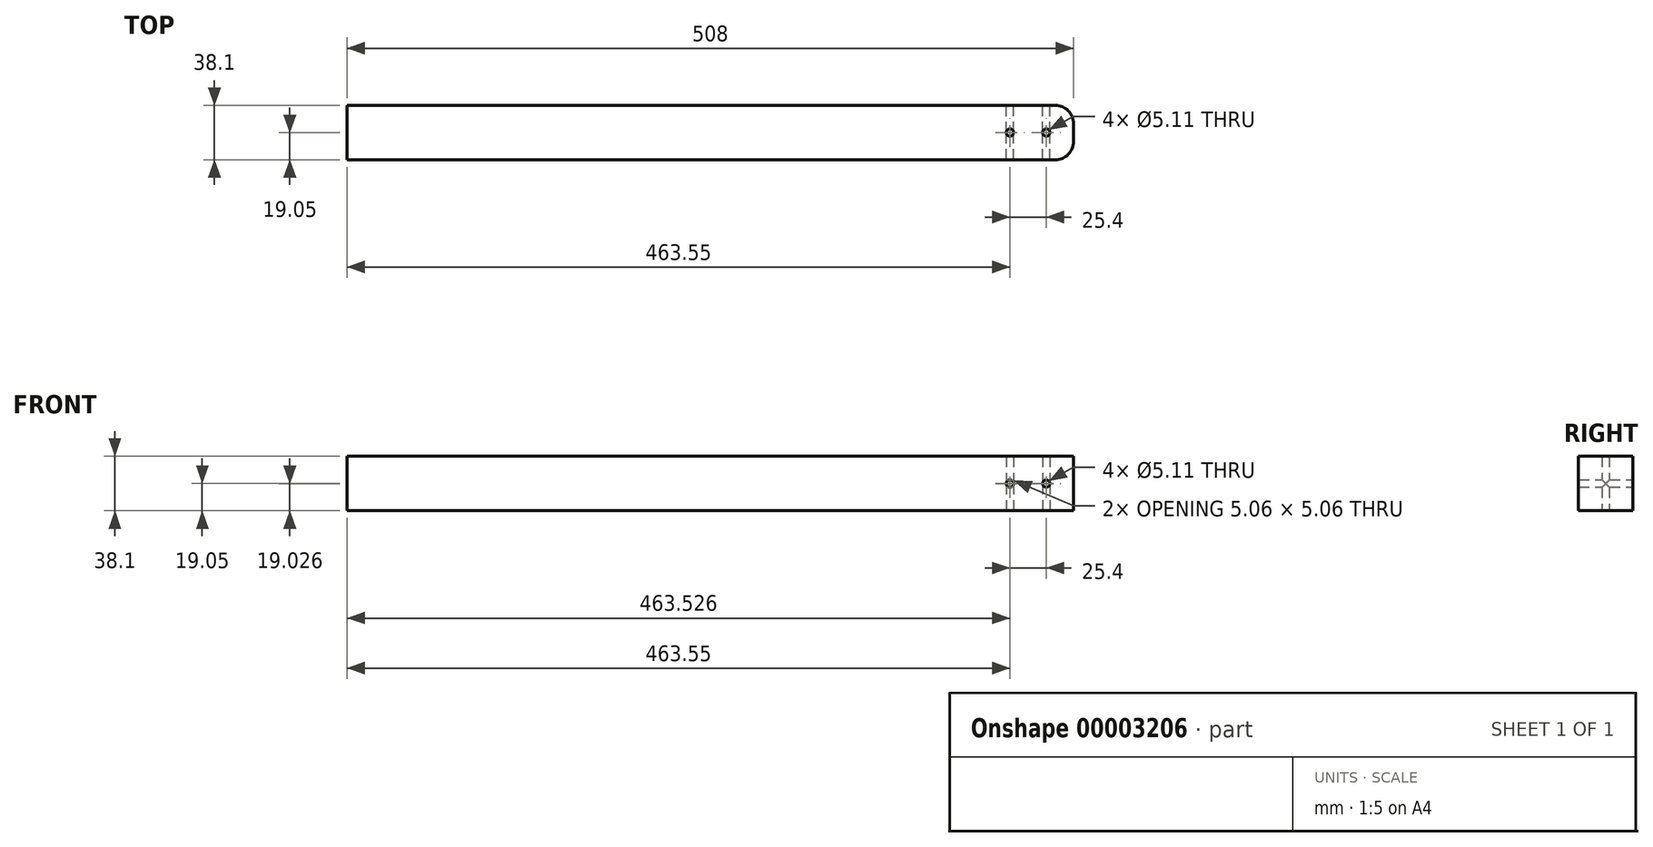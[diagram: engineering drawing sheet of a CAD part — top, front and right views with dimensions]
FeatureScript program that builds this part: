
annotation { "Feature Type Name" : "Feature", "Feature Type Description" : "" }
export const myFeature = defineFeature(function(context is Context, id is Id, definition is map)
    precondition{}
    {
        {
            var Q0;
            Q0=qCreatedBy(makeId("Front.planeOp"),FACE);
            var sketch = newSketch(context, id + "F0", { "sketchPlane" : qUnion([Q0])});
            skLineSegment(sketch, "E0", {"start": v(0, 0) * mm, "end": v(0, -38.1) * mm});
            skLineSegment(sketch, "E1", {"start": v(0, -38.1) * mm, "end": v(508, -38.1) * mm});
            skLineSegment(sketch, "E2", {"start": v(508, -38.1) * mm, "end": v(508, 0) * mm});
            skLineSegment(sketch, "E3", {"start": v(508, 0) * mm, "end": v(0, 0) * mm});
            skLineSegment(sketch, "E4", {"start": v(508, -19.05) * mm, "end": v(320.2, -19.05) * mm, "construction": true});
            skLineSegment(sketch, "E5", {"start": v(488.95, 0) * mm, "end": v(488.95, -38.1) * mm, "construction": true});
            skLineSegment(sketch, "E6", {"start": v(463.55, 0) * mm, "end": v(463.55, -38.1) * mm, "construction": true});
            skCircle(sketch, "E7", {"center": v(463.55, -19.05) * mm, "radius": 2.55 * mm});
            skCircle(sketch, "E8", {"center": v(488.95, -19.05) * mm, "radius": 2.55 * mm});
            skSolve(sketch);
        }
        {
            var Q0;
            Q0=makeQuery(id+"F0.imprint","IMPRINT",FACE,{"disambiguationData":[TD([[makeQuery(id+"F0.imprint","IMPRINT",EDGE,{"derivedFrom":sQuery(id+"F0.wireOp",EDGE,"E0")}),1.0]])]});
            extrude(context, id + "F1", {"entities" : qUnion([Q0]), "endBound" : BoundingType.SYMMETRIC, "depth" : 38.1 * mm});
        }
        {
            var Q0;
            Q0=makeQuery(id+"F1.opExtrude","SWEPT_FACE",FACE,{"disambiguationData":[OSD([sQuery(id+"F0.wireOp",EDGE,"E1")])]});
            var sketch = newSketch(context, id + "F2", { "sketchPlane" : qUnion([Q0])});
            skLineSegment(sketch, "E9", {"start": v(508, 0) * mm, "end": v(309.48, 0) * mm, "construction": true});
            skLineSegment(sketch, "E10", {"start": v(488.95, 19.05) * mm, "end": v(488.95, -19.05) * mm, "construction": true});
            skLineSegment(sketch, "E11", {"start": v(463.55, 19.05) * mm, "end": v(463.55, -19.05) * mm, "construction": true});
            skCircle(sketch, "E12", {"center": v(463.55, 0) * mm, "radius": 2.55 * mm});
            skCircle(sketch, "E13", {"center": v(488.95, 0) * mm, "radius": 2.55 * mm});
            skSolve(sketch);
        }
        {
            var Q0;
            Q0=makeQuery(id+"F2.imprint","IMPRINT",FACE,{"disambiguationData":[TD([[makeQuery(id+"F2.imprint","IMPRINT",EDGE,{"derivedFrom":sQuery(id+"F2.wireOp",EDGE,"E13")}),1.0]])]});
            var Q1;
            Q1=makeQuery(id+"F2.imprint","IMPRINT",FACE,{"disambiguationData":[TD([[makeQuery(id+"F2.imprint","IMPRINT",EDGE,{"derivedFrom":sQuery(id+"F2.wireOp",EDGE,"E12")}),1.0]])]});
            extrude(context, id + "F3", {"entities" : qUnion([Q0, Q1]), "operationType" : NewBodyOperationType.REMOVE, "endBound" : BoundingType.THROUGH_ALL, "oppositeDirection" : true, "depth" : 25.4 * mm});
        }
        {
            var Q0;
            Q0=makeQuery(id+"F1.opExtrude","CAP_EDGE",EDGE,{"disambiguationData":[OSD([sQuery(id+"F0.wireOp",EDGE,"E2")])],"isStart":true});
            var Q1;
            Q1=makeQuery(id+"F1.opExtrude","CAP_EDGE",EDGE,{"disambiguationData":[OSD([sQuery(id+"F0.wireOp",EDGE,"E2")])],"isStart":false});
            fillet(context, id + "F4", {"entities" : qUnion([Q0, Q1]), "radius" : 12.7 * mm, "tangentPropagation" : true, "allowEdgeOverflow" : false});
        }
    });
